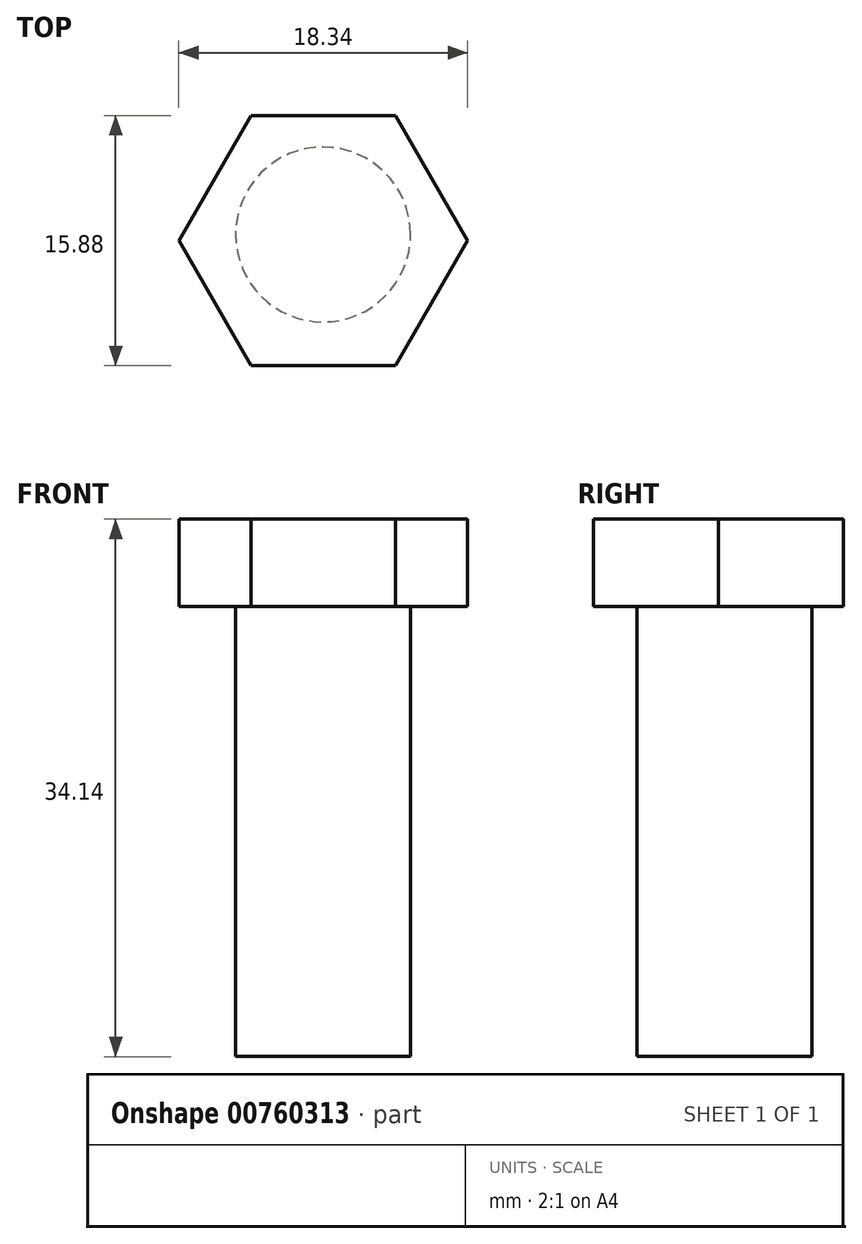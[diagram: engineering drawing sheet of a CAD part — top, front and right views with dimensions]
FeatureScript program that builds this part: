
annotation { "Feature Type Name" : "Feature", "Feature Type Description" : "" }
export const myFeature = defineFeature(function(context is Context, id is Id, definition is map)
    precondition{}
    {
        {
            var Q0;
            Q0=qCreatedBy(makeId("Top.planeOp"),FACE);
            var sketch = newSketch(context, id + "F0", { "sketchPlane" : qUnion([Q0])});
            skCircle(sketch, "E0.cCircle", {"center": v(0, 0) * mm, "radius": 7.94 * mm, "construction": true});
            skLineSegment(sketch, "E0.0", {"start": v(-4.58, 7.94) * mm, "end": v(4.58, 7.94) * mm});
            skLineSegment(sketch, "E0.1", {"start": v(4.58, 7.94) * mm, "end": v(9.17, 0) * mm});
            skLineSegment(sketch, "E0.2", {"start": v(9.17, 0) * mm, "end": v(4.58, -7.94) * mm});
            skLineSegment(sketch, "E0.3", {"start": v(4.58, -7.94) * mm, "end": v(-4.58, -7.94) * mm});
            skLineSegment(sketch, "E0.4", {"start": v(-4.58, -7.94) * mm, "end": v(-9.17, 0) * mm});
            skLineSegment(sketch, "E0.5", {"start": v(-9.17, 0) * mm, "end": v(-4.58, 7.94) * mm});
            skPoint(sketch, "E0.0.midPoint", {"position": v(0, 7.94) * mm});
            skSolve(sketch);
        }
        {
            var Q0;
            Q0=qCreatedBy(makeId("Top.planeOp"),FACE);
            var sketch = newSketch(context, id + "F1", { "sketchPlane" : qUnion([Q0])});
            skCircle(sketch, "E1", {"center": v(0, 0.4) * mm, "radius": 5.56 * mm});
            skSolve(sketch);
        }
        {
            var Q0;
            Q0 = qSketchRegion(id + "F0", true);
            extrude(context, id + "F2", {"entities" : qUnion([Q0]), "depth" : 5.56 * mm, "offsetDistance" : 25.4 * mm});
        }
        {
            var Q0;
            Q0 = qSketchRegion(id + "F1", true);
            extrude(context, id + "F3", {"entities" : qUnion([Q0]), "operationType" : NewBodyOperationType.ADD, "oppositeDirection" : true, "depth" : 28.57 * mm, "offsetDistance" : 25.4 * mm});
        }
    });
